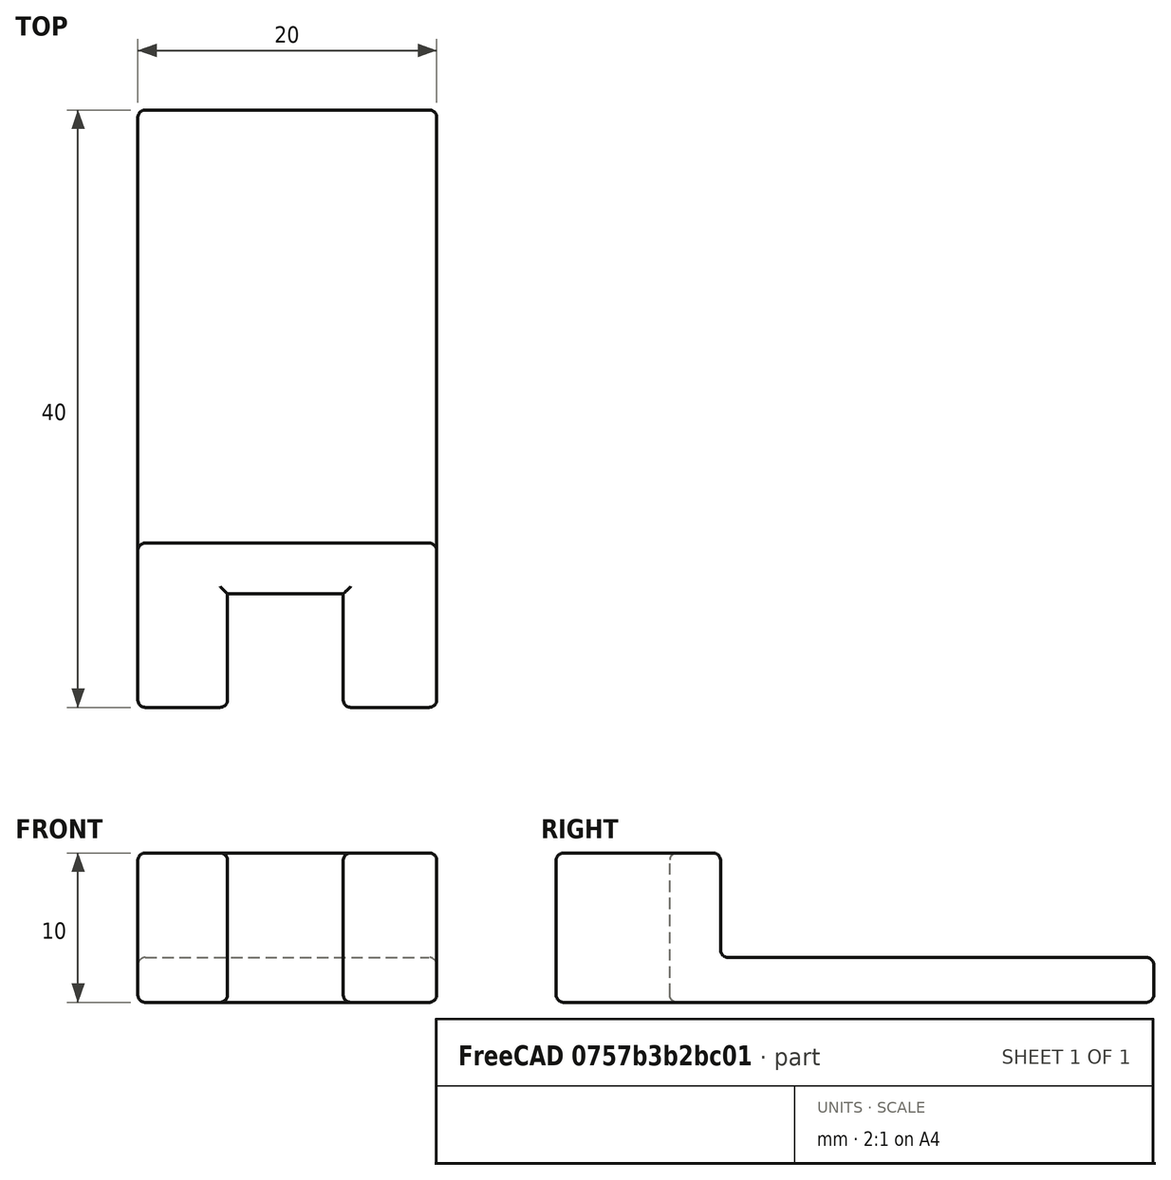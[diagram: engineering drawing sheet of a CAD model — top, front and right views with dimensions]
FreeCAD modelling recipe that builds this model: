
FCSTD DOCUMENT  (FreeCAD 0.18R16146 (Git))
Label: Stuetzenhalter
License: All rights reserved
LicenseURL: http://en.wikipedia.org/wiki/All_rights_reserved
objects: Part::Box×3, Part::Cut×2, Part::Fillet×1
note: 6 computed .brp shape members not serialized (recipe doc carries the construction recipe); baked Part::Feature solids carry a one-line shape summary decoded from their .brp

FEATURE [Part::Box] Box  label="Cube"
  AttacherType = Attacher::AttachEngine3D
  Height = 10
  Length = 7.75
  Placement = pos=(6,0,0) rot=(0,0,1;0rad)
  Width = 7.6
FEATURE [Part::Box] Box001  label="Cube001"
  AttacherType = Attacher::AttachEngine3D
  Height = 10
  Length = 20
  Width = 40
FEATURE [Part::Cut] Cut
  Base = -> Box001
  Tool = -> Box
FEATURE [Part::Box] Box002  label="Cube002"
  AttacherType = Attacher::AttachEngine3D
  Height = 10
  Length = 20
  Placement = pos=(0,11,3) rot=(0,0,1;0rad)
  Width = 30
FEATURE [Part::Cut] Cut001
  Base = -> Cut
  Tool = -> Box002
FEATURE [Part::Fillet] Fillet
  Base = -> Cut001
  Edges = 28 edges r=0.5: [Edge1,Edge2,Edge3,Edge4,Edge5,Edge6,Edge7,Edge8,Edge9,Edge10,Edge11,Edge12,Edge13,Edge14,Edge15,Edge16,Edge17,Edge18,Edge19,Edge20,Edge21,Edge22,Edge23,Edge24,Edge25,Edge26,Edge27,Edge28]
